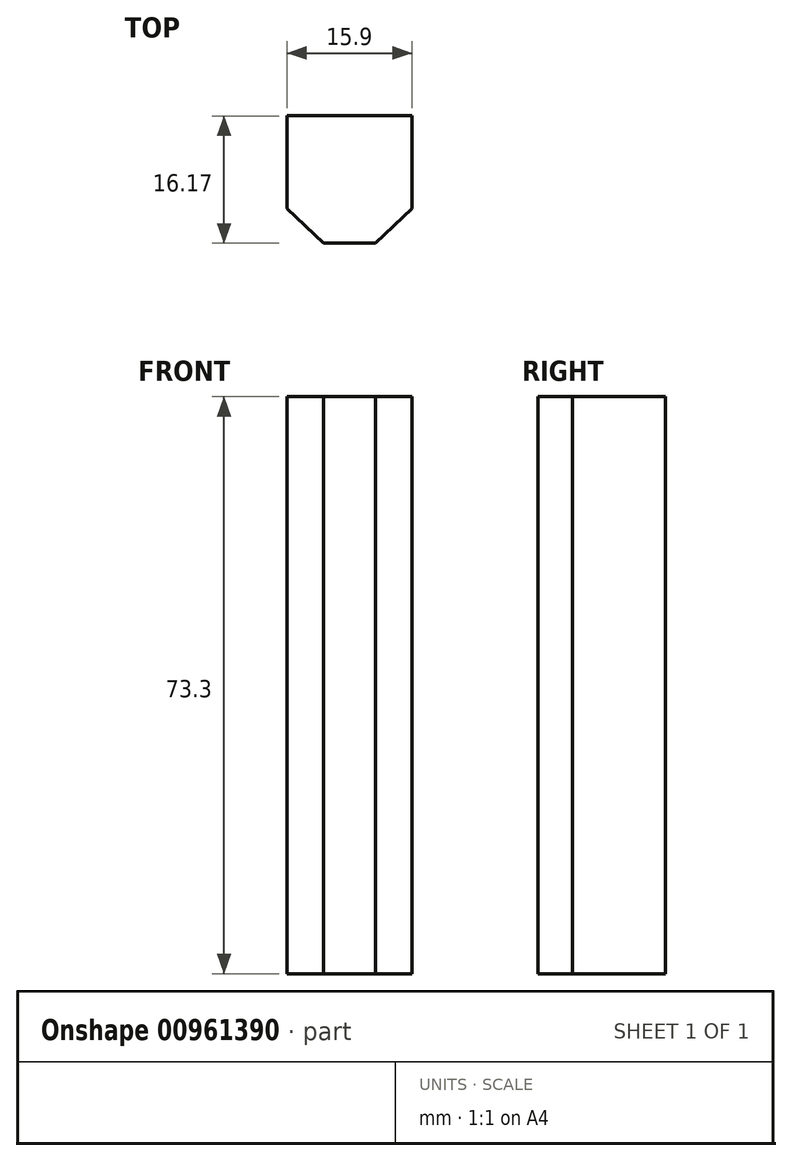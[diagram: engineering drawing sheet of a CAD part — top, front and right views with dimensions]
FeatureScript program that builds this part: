
annotation { "Feature Type Name" : "Feature", "Feature Type Description" : "" }
export const myFeature = defineFeature(function(context is Context, id is Id, definition is map)
    precondition{}
    {
        {
            var Q0;
            Q0=qCreatedBy(makeId("Top.planeOp"),FACE);
            var sketch = newSketch(context, id + "F0", { "sketchPlane" : qUnion([Q0])});
            skLineSegment(sketch, "E0", {"start": v(0, 18.63) * mm, "end": v(0, -13.83) * mm, "construction": true});
            skLineSegment(sketch, "E1", {"start": v(0, 11.68) * mm, "end": v(-7.95, 11.68) * mm});
            skLineSegment(sketch, "E2", {"start": v(-7.95, 11.68) * mm, "end": v(-7.95, -0.12) * mm});
            skLineSegment(sketch, "E3", {"start": v(-7.95, -0.12) * mm, "end": v(-3.3, -4.49) * mm});
            skLineSegment(sketch, "E4", {"start": v(-3.31, -4.49) * mm, "end": v(0, -4.49) * mm});
            skLineSegment(sketch, "E5.MirrorCS", {"start": v(0, 11.68) * mm, "end": v(7.95, 11.68) * mm});
            skLineSegment(sketch, "E6.MirrorCS", {"start": v(7.95, 11.68) * mm, "end": v(7.95, -0.12) * mm});
            skLineSegment(sketch, "E7.MirrorCS", {"start": v(7.95, -0.12) * mm, "end": v(3.3, -4.49) * mm});
            skLineSegment(sketch, "E8.MirrorCS", {"start": v(3.31, -4.49) * mm, "end": v(0, -4.49) * mm});
            skSolve(sketch);
        }
        {
            var Q0;
            Q0 = qSketchRegion(id + "F0", true);
            extrude(context, id + "F1", {"entities" : qUnion([Q0]), "depth" : 73.3 * mm, "offsetDistance" : 25 * mm});
        }
    });
